# Revit family: 05-9912-Z5-CM
name_source: partatom
category: Luminarias
revit_build: Autodesk Revit 2017 (Build: 20160225_1515(x64)
units: mm (PartAtom-declared; Revit-internal decimal feet)

## family parameters
Anfitrión = Cara
Compartido = Sí
Corte con vacíos al cargar = No
Cota de conector redondo = Diámetro de uso
Número OmniClass = 23.80.70.00
Origen de luz = No
Punto de cálculo de habitación = No
Tipo de pieza = Normal
Título OmniClass = Lighting

## types (1)
- 05-9912-Z5-CM
    Acabado = Gris urbano, Semi arenado
    CRI = 80
    Carga aparente = 0 VA
    Catálogo = Outdoor
    CodigoGubimclass = 50.60.50.20
    CodigoOmniclass = 21-04 50 40
    CodigoUniclass2015 = EF_70_80
    CodigoUniformat2010 = D5040
    DescripcionGubimclass = Iluminación interior
    DescripcionOmniclass = Lighting
    DescripcionUniclass2015 = Lighting
    DescripcionUniformat2010 = Lighting
    EAN13 = 8435381496302
    Eficiencia energética = LED A++
    Elevación por defecto = 1000 mm  [stored 3.28084 ft]
    Etiqueta V/f = 100-240V/50-60Hz
    Fabricante = LEDS C4
    Familia = Afrodita LED 220mm One Emission
    FechaVersion = Julio 2020
    Ficha = http://files.leds-c4.com
    Fotometría = http://files.leds-c4.com
    Fuente de luz = 10xLED 11.5 1217.00 lm
    IK = IK04
    IMC = http://files.leds-c4.com
    IP = IP65
    IfcExportAs = IfcLightFixture
IfcLightFixture
    IfcExportType = NOTDEFINED
    Imagen web = http://files.leds-c4.com
    LDT = http://files.leds-c4.com
    Lumenes reales (lm) = 1004
    Material = Aluminio, Cristal
    Peso neto (KG) = 1.39
    Pluma comercial = http://files.leds-c4.com
    Producto descatalogado = Catalogado ES
    Rayo de luz = Check Photometric file
    Referencia = 05-9912-Z5-CM
    Temperatura color led (K) = Blanco neutro - 4000K
    Tender text (Castellano) = LEDS C4
Afrodita LED 220mm One Emission
05-9912-Z5-CM

Aplique de uso interior y exterior para iluminar hacia abajo. 
Material estructura: Aluminio. Acabado estructura: Gris urbano. Material difusor: Cristal. Acabado difusor: Semi arenado. Protección contra los rayos ultravioleta. Garantía: 5 Años.

Peso neto del producto (Kg): 1.390
Anchura o diámetro del producto (mm): 220
Altura del producto (mm): 90
Salida del producto (mm): 120

Clase 1. Prueba hilo incandescente: 850. IP: IP65. IK: IK04. LED. Nº de portalámparas o Leds: 10. Marca del LED: LEXTAR. Marca del Driver: EAGLERISE. Potencia máxima de la fuente de luz: 11.5W. Temperatura de color: Blanco neutro - 4000K. Índice de reproducción cromática: 80. Steps Mac Adam: 3. Diámetro máximo de la bombilla que admite la luminaria: 50.000h L80B20. UGR:  22.5. Riesgo fotobiológico: RG0. Flujo real (lm): 1004. Flujo nominal (lm): 1217. Lm/W reales: 79. Rango de voltaje/frecuencia: 100-240/50-60Hz. Voltaje: 6. Equipo incluido: Si, electrónico. Equipo multivoltaje incluido. Potencia total: 12.7. Factor de potencia: 0.90.
    Tender text (English) = LEDS C4
Afrodita LED 220mm One Emission
05-9912-Z5-CM

Wall light for indoor and outdoor use. 

For downlighting. Structure material: Aluminium. Structure finish: Urban grey. Diffuser material: Glass. Diffuser finish: Partly-sandblasted. UV protection. Warranty: 5 Years.

Product net weight (Kg): 1.390
Product width or diameter (mm): 220
Product height (mm): 90
Product aperture (mm): 120

Class 1. Glow wire test: 850. IP: IP65. IK: IK04. LED. No. of lampholders or LEDs: 10. LED brand: LEXTAR. Driver brand: EAGLERISE. Maximum power of light source: 11.5W. Colour temperature: LED neutral-white 4000K. Colour rendering index: 80. MacAdam Steps: 3. Maximum diameter of luminaire bulb: 50.000h L80B20. UGR:  22.5. Photobiological risk: RG0. Real flux (lm): 1004. Nominal flux (lm): 1217. Lm/Real W: 79. Voltage and frequency range: 100-240/50-60Hz. Voltage: 6. Gear included: Yes, electronic. Multi-voltage gear included. Total power: 12.7. Power factor: 0.90.
    Tipo = Aplique
    Vatios (W) = 12.7
    Versión = v1

note: [stored X ft] marks values corroborated as IEEE doubles in the binary element streams (Revit-internal decimal feet)
